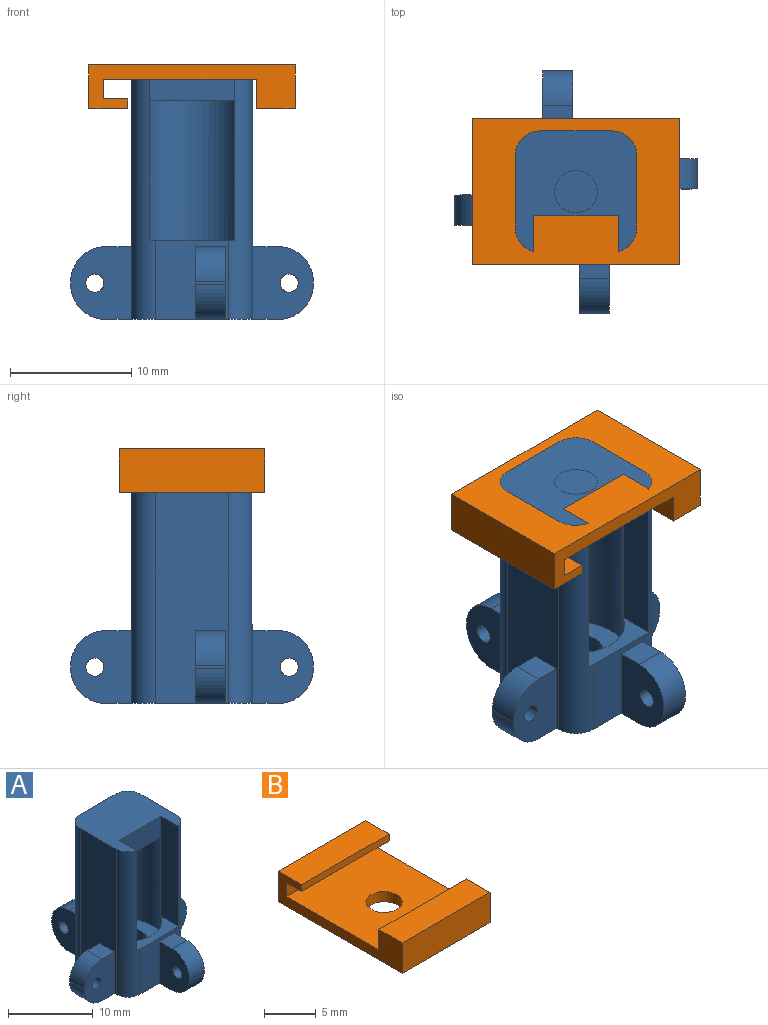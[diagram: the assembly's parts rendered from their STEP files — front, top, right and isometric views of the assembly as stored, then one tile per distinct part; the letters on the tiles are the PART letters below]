
ASSEMBLY  parts=2 mates=1
PART A: 46 faces, bbox 20x20x21 mm
  f0: plane 6.53x6mm, normal (0,-1,0), area 24.2mm2, adj f8,f21,f22,f23,f26,f27,f38
  f1: plane 10x9.94mm, normal (0,0,1), area 75.6mm2, adj f5,f6,f7,f25,f26,f27,f28,f39
  f2: cylinder r=4mm len=14mm, axis (0,0,1), area 255.7mm2, adj f3,f37,f38,f39
  f3: plane 8x6mm, normal (0,0,-1), area 40.4mm2, adj f2,f39
  f4: cylinder r=2.25mm len=4.5mm, axis (0,0,-1), area 56.5mm2, adj f8,f37
  f5: plane 21x6mm, normal (1,0,0), area 111mm2, adj f1,f8,f17,f18,f19,f27,f28
  f6: plane 21x6mm, normal (0,1,0), area 111mm2, adj f1,f8,f13,f14,f15,f25,f28
  f7: plane 21x6mm, normal (-1,0,0), area 111mm2, adj f1,f8,f9,f10,f11,f25,f26
  f8: plane 14.21x14.21mm, normal (0,0,-1), area 101.7mm2, adj f0,f4,f5,f6,f7,f9,f10,f13
  f9: plane 6x5mm, normal (0,1,0), area 24.6mm2, adj f7,f8,f11,f12,f35,f36,f43
  f10: plane 6x5mm, normal (0,-1,0), area 24.6mm2, adj f7,f8,f11,f12,f35,f36,f43
  f11: plane 2.5x2.1mm, normal (0,0,1), area 5.3mm2, adj f7,f9,f10,f36
  f12: plane 2.5x0.21mm, normal (-1,0,0), area 0.5mm2, adj f9,f10,f35,f36
  f13: plane 6x5mm, normal (1,0,0), area 24.6mm2, adj f6,f8,f15,f16,f33,f34,f44
  f14: plane 6x5mm, normal (-1,0,0), area 24.6mm2, adj f6,f8,f15,f16,f33,f34,f44
  f15: plane 2.5x2.1mm, normal (0,0,1), area 5.3mm2, adj f6,f13,f14,f34
  f16: plane 2.5x0.21mm, normal (0,1,0), area 0.5mm2, adj f13,f14,f33,f34
  f17: plane 6x5mm, normal (0,-1,0), area 24.6mm2, adj f5,f8,f19,f20,f31,f32,f45
  f18: plane 6x5mm, normal (0,1,0), area 24.6mm2, adj f5,f8,f19,f20,f31,f32,f45
  f19: plane 2.5x2.1mm, normal (0,0,1), area 5.3mm2, adj f5,f17,f18,f32
  f20: plane 2.5x0.21mm, normal (1,0,0), area 0.5mm2, adj f17,f18,f31,f32
  f21: plane 6x5mm, normal (-1,0,0), area 24.6mm2, adj f0,f8,f23,f24,f29,f30,f42
  f22: plane 6x5mm, normal (1,0,0), area 24.6mm2, adj f0,f8,f23,f24,f29,f30,f42
  f23: plane 2.5x2.1mm, normal (0,0,1), area 5.3mm2, adj f0,f21,f22,f30
  f24: plane 2.5x0.21mm, normal (0,-1,0), area 0.5mm2, adj f21,f22,f29,f30
  f25: cylinder r=2mm len=21mm, axis (0,0,1), area 66mm2, adj f1,f6,f7,f8
  f26: cylinder r=2mm len=21mm, axis (0,0,-1), area 58.7mm2, adj f0,f1,f7,f8,f38,f41
  f27: cylinder r=2mm len=21mm, axis (0,0,1), area 58.7mm2, adj f0,f1,f5,f8,f38,f40
  f28: cylinder r=2mm len=21mm, axis (0,0,-1), area 66mm2, adj f1,f5,f6,f8
  f29: cylinder r=2.9mm len=2.9mm, axis (-1,0,0), area 11.4mm2, adj f8,f21,f22,f24
  f30: cylinder r=2.9mm len=2.9mm, axis (1,0,0), area 11.4mm2, adj f21,f22,f23,f24
  f31: cylinder r=2.9mm len=2.9mm, axis (0,1,0), area 11.4mm2, adj f8,f17,f18,f20
  f32: cylinder r=2.9mm len=2.9mm, axis (0,1,0), area 11.4mm2, adj f17,f18,f19,f20
  f33: cylinder r=2.9mm len=2.9mm, axis (-1,0,0), area 11.4mm2, adj f8,f13,f14,f16
  f34: cylinder r=2.9mm len=2.9mm, axis (-1,0,0), area 11.4mm2, adj f13,f14,f15,f16
  f35: cylinder r=2.9mm len=2.9mm, axis (0,1,0), area 11.4mm2, adj f8,f9,f10,f12
  f36: cylinder r=2.9mm len=2.9mm, axis (0,-1,0), area 11.4mm2, adj f9,f10,f11,f12
  f37: plane 8x8mm, normal (0,0,1), area 34.4mm2, adj f2,f4
  f38: plane 7x3mm, normal (0,0,1), area 11.2mm2, adj f0,f2,f26,f27,f39,f40,f41
  f39: plane 14.47x7mm, normal (0,-1,0), area 21.8mm2, adj f1,f2,f3,f38,f40,f41
  f40: plane 14.47x2.94mm, normal (-1,0,0), area 42.5mm2, adj f1,f27,f38,f39
  f41: plane 14.47x2.94mm, normal (1,0,0), area 42.5mm2, adj f1,f26,f38,f39
  f42: cylinder r=0.75mm len=2.5mm, axis (1,0,0), area 11.8mm2, adj f21,f22
  f43: cylinder r=0.75mm len=2.5mm, axis (0,-1,0), area 11.8mm2, adj f9,f10
  f44: cylinder r=0.75mm len=2.5mm, axis (-1,0,0), area 11.8mm2, adj f13,f14
  f45: cylinder r=0.75mm len=2.5mm, axis (0,1,0), area 11.8mm2, adj f17,f18
PART B: 13 faces, bbox 12x17x3.6 mm
  f0: plane 12x0.8mm, normal (0,-1,0), area 9.6mm2, adj f1,f4,f8,f11
  f1: plane 17x3.6mm, normal (1,0,0), area 32.6mm2, adj f0,f2,f3,f5,f6,f8,f9,f10
  f2: plane 12.6x12mm, normal (0,0,1), area 141.6mm2, adj f1,f4,f7,f9,f12
  f3: plane 12x3.6mm, normal (0,1,0), area 43.2mm2, adj f1,f4,f6,f8
  f4: plane 17x3.6mm, normal (-1,0,0), area 32.6mm2, adj f0,f2,f3,f5,f6,f8,f9,f10
  f5: plane 12x3.6mm, normal (0,-1,0), area 43.2mm2, adj f1,f4,f6,f10
  f6: plane 17x12mm, normal (0,0,-1), area 194.4mm2, adj f1,f3,f4,f5,f7
  f7: cylinder r=1.75mm len=3.5mm, axis (0,0,1), area 13.2mm2, adj f2,f6
  f8: plane 12x3.2mm, normal (0,0,1), area 38.4mm2, adj f0,f1,f3,f4
  f9: plane 12x2.4mm, normal (0,1,0), area 28.8mm2, adj f1,f2,f4,f10
  f10: plane 12x3.2mm, normal (0,0,1), area 38.4mm2, adj f1,f4,f5,f9
  f11: plane 12x2mm, normal (0,0,-1), area 24mm2, adj f0,f1,f4,f12
  f12: plane 12x1.6mm, normal (0,-1,0), area 19.2mm2, adj f1,f2,f4,f11
PLACE A t=(-9.92,19.64,-4.22)mm fixed
PLACE B rot(axis=(0.71,-0.71,0),180deg) t=(-9.92,19.64,16.75)mm
MATE slider B.f7 <-> A.f2  axis (0,0,1) through (-9.92,19.64,16.75)mm
